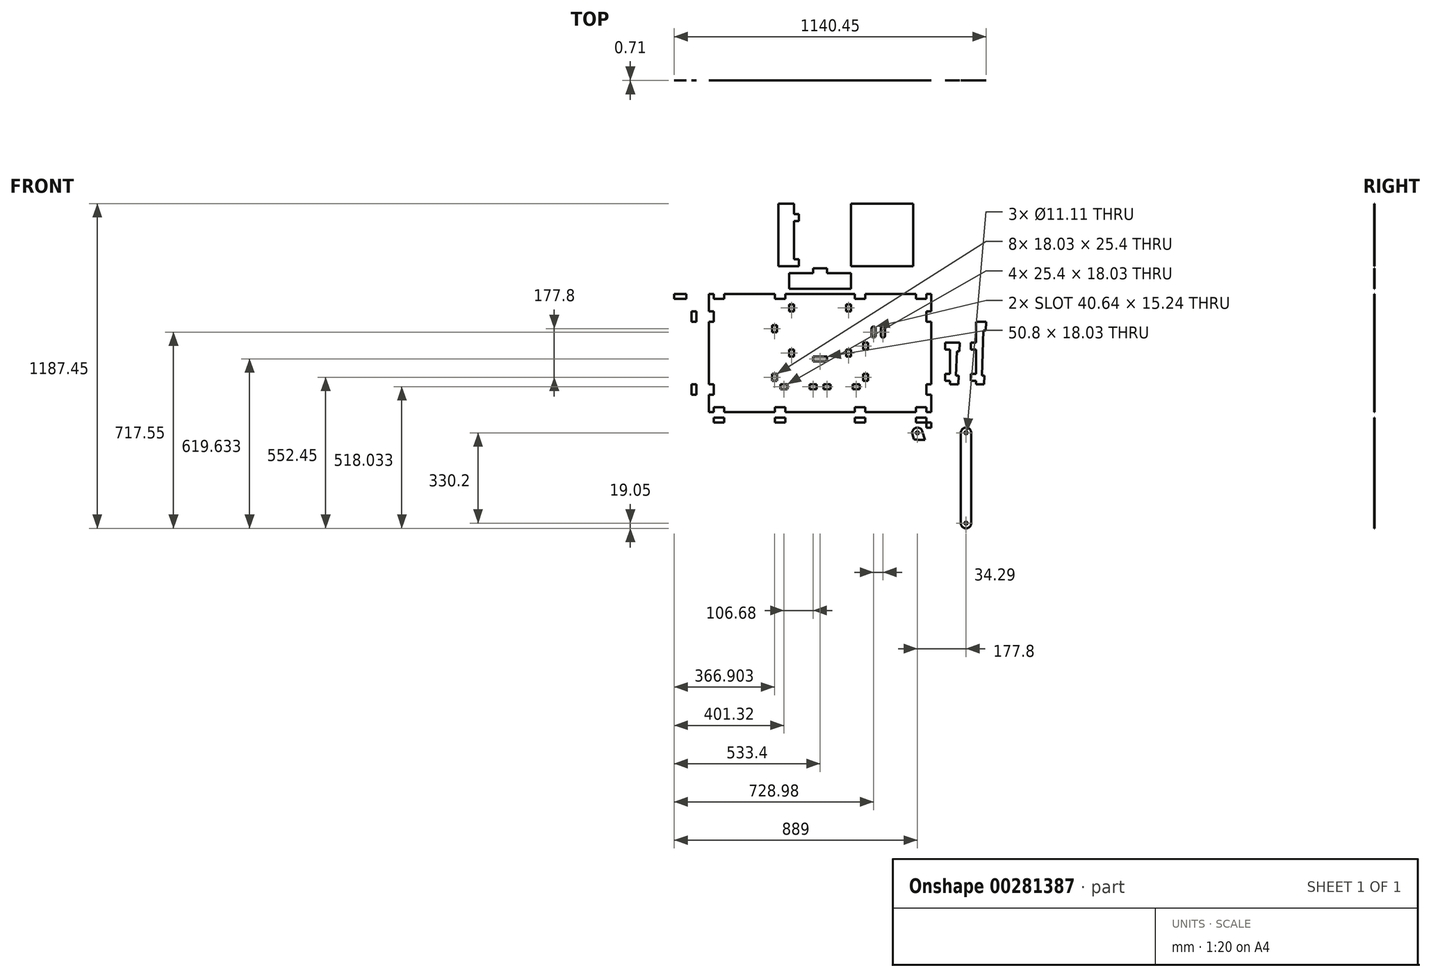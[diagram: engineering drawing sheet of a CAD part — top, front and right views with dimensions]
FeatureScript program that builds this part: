
annotation { "Feature Type Name" : "Feature", "Feature Type Description" : "" }
export const myFeature = defineFeature(function(context is Context, id is Id, definition is map)
    precondition{}
    {
        {
            assignVariable(context, id + "F0", {"name" : "ply34", "anyValue" : .71});
        }
        {
            var Q0;
            Q0=qCreatedBy(makeId("Front.planeOp"),FACE);
            var sketch = newSketch(context, id + "F1", { "sketchPlane" : qUnion([Q0])});
            skLineSegment(sketch, "E0.bottom", {"start": v(-406.4, 215.9) * mm, "end": v(406.4, 215.9) * mm});
            skLineSegment(sketch, "E0.top", {"start": v(-406.4, -215.9) * mm, "end": v(406.4, -215.9) * mm});
            skLineSegment(sketch, "E0.left", {"start": v(-406.4, 215.9) * mm, "end": v(-406.4, -215.9) * mm});
            skLineSegment(sketch, "E0.right", {"start": v(406.4, 215.9) * mm, "end": v(406.4, -215.9) * mm});
            skPoint(sketch, "E0.middle", {"position": v(0, 0) * mm});
            skLineSegment(sketch, "E1.bottom", {"start": v(-157.48, 114.3) * mm, "end": v(157.48, 114.3) * mm, "construction": true});
            skLineSegment(sketch, "E1.top", {"start": v(-157.48, -114.3) * mm, "end": v(157.48, -114.3) * mm, "construction": true});
            skLineSegment(sketch, "E1.left", {"start": v(-157.48, 114.3) * mm, "end": v(-157.48, -114.3) * mm, "construction": true});
            skLineSegment(sketch, "E1.right", {"start": v(157.48, 114.3) * mm, "end": v(157.48, -114.3) * mm, "construction": true});
            skLineSegment(sketch, "E2.bottom", {"start": v(-12.7, -114.3) * mm, "end": v(12.7, -114.3) * mm, "construction": true});
            skLineSegment(sketch, "E2.top", {"start": v(-12.7, 114.3) * mm, "end": v(12.7, 114.3) * mm, "construction": true});
            skLineSegment(sketch, "E2.left", {"start": v(-12.7, -114.3) * mm, "end": v(-12.7, 114.3) * mm, "construction": true});
            skLineSegment(sketch, "E2.right", {"start": v(12.7, -114.3) * mm, "end": v(12.7, 114.3) * mm, "construction": true});
            skLineSegment(sketch, "E3.bottom", {"start": v(157.48, 12.7) * mm, "end": v(175.51, 12.7) * mm});
            skLineSegment(sketch, "E3.top", {"start": v(157.48, 38.1) * mm, "end": v(175.51, 38.1) * mm});
            skLineSegment(sketch, "E3.left", {"start": v(157.48, 12.7) * mm, "end": v(157.48, 38.1) * mm});
            skLineSegment(sketch, "E3.right", {"start": v(175.51, 12.7) * mm, "end": v(175.51, 38.1) * mm});
            skLineSegment(sketch, "E4.bottom", {"start": v(157.48, -101.6) * mm, "end": v(175.51, -101.6) * mm});
            skLineSegment(sketch, "E4.top", {"start": v(157.48, -76.2) * mm, "end": v(175.51, -76.2) * mm});
            skLineSegment(sketch, "E4.left", {"start": v(157.48, -101.6) * mm, "end": v(157.48, -76.2) * mm});
            skLineSegment(sketch, "E4.right", {"start": v(175.51, -101.6) * mm, "end": v(175.51, -76.2) * mm});
            skLineSegment(sketch, "E5.bottom", {"start": v(-157.48, 101.6) * mm, "end": v(-175.51, 101.6) * mm});
            skLineSegment(sketch, "E5.top", {"start": v(-157.48, 76.2) * mm, "end": v(-175.51, 76.2) * mm});
            skLineSegment(sketch, "E5.left", {"start": v(-157.48, 101.6) * mm, "end": v(-157.48, 76.2) * mm});
            skLineSegment(sketch, "E5.right", {"start": v(-175.51, 101.6) * mm, "end": v(-175.51, 76.2) * mm});
            skLineSegment(sketch, "E6.bottom", {"start": v(-157.48, -76.2) * mm, "end": v(-175.51, -76.2) * mm});
            skLineSegment(sketch, "E6.top", {"start": v(-157.48, -101.6) * mm, "end": v(-175.51, -101.6) * mm});
            skLineSegment(sketch, "E6.left", {"start": v(-157.48, -76.2) * mm, "end": v(-157.48, -101.6) * mm});
            skLineSegment(sketch, "E6.right", {"start": v(-175.51, -76.2) * mm, "end": v(-175.51, -101.6) * mm});
            skLineSegment(sketch, "E7", {"start": v(195.58, 88.9) * mm, "end": v(195.58, 63.5) * mm});
            skLineSegment(sketch, "E8", {"start": v(229.87, 88.9) * mm, "end": v(229.87, 63.5) * mm});
            skArc(sketch, "E9.0.startCap", {"start": v(187.96, 88.9) * mm, "mid": v(195.58, 96.52) * mm, "end": v(203.2, 88.9) * mm});
            skArc(sketch, "E9.0.endCap", {"start": v(203.2, 63.5) * mm, "mid": v(195.58, 55.88) * mm, "end": v(187.96, 63.5) * mm});
            skLineSegment(sketch, "E9.0.left", {"start": v(203.2, 88.9) * mm, "end": v(203.2, 63.5) * mm});
            skLineSegment(sketch, "E9.0.right", {"start": v(187.96, 88.9) * mm, "end": v(187.96, 63.5) * mm});
            skArc(sketch, "E9.1.startCap", {"start": v(222.25, 88.9) * mm, "mid": v(229.87, 96.52) * mm, "end": v(237.49, 88.9) * mm});
            skArc(sketch, "E9.1.endCap", {"start": v(237.5, 63.5) * mm, "mid": v(229.87, 55.88) * mm, "end": v(222.25, 63.5) * mm});
            skLineSegment(sketch, "E9.1.left", {"start": v(237.49, 88.9) * mm, "end": v(237.49, 63.5) * mm});
            skLineSegment(sketch, "E9.1.right", {"start": v(222.25, 88.9) * mm, "end": v(222.25, 63.5) * mm});
            skLineSegment(sketch, "E10.bottom", {"start": v(-388.37, -215.9) * mm, "end": v(-350.27, -215.9) * mm});
            skLineSegment(sketch, "E10.top", {"start": v(-388.37, -197.87) * mm, "end": v(-350.27, -197.87) * mm});
            skLineSegment(sketch, "E10.left", {"start": v(-388.37, -215.9) * mm, "end": v(-388.37, -197.87) * mm});
            skLineSegment(sketch, "E10.right", {"start": v(-350.27, -215.9) * mm, "end": v(-350.27, -197.87) * mm});
            skLineSegment(sketch, "E11", {"start": v(0, -215.9) * mm, "end": v(0, 215.9) * mm, "construction": true});
            skLineSegment(sketch, "E12.bottom", {"start": v(-165.1, -215.9) * mm, "end": v(-127, -215.9) * mm});
            skLineSegment(sketch, "E12.top", {"start": v(-165.1, -197.87) * mm, "end": v(-127, -197.87) * mm});
            skLineSegment(sketch, "E12.left", {"start": v(-165.1, -215.9) * mm, "end": v(-165.1, -197.87) * mm});
            skLineSegment(sketch, "E12.right", {"start": v(-127, -215.9) * mm, "end": v(-127, -197.87) * mm});
            skLineSegment(sketch, "E13.MirrorCS", {"start": v(350.27, -215.9) * mm, "end": v(350.27, -197.87) * mm});
            skLineSegment(sketch, "E14.MirrorCS", {"start": v(127, -215.9) * mm, "end": v(127, -197.87) * mm});
            skLineSegment(sketch, "E15.MirrorCS", {"start": v(165.1, -215.9) * mm, "end": v(127, -215.9) * mm});
            skLineSegment(sketch, "E16.MirrorCS", {"start": v(388.37, -215.9) * mm, "end": v(388.37, -197.87) * mm});
            skLineSegment(sketch, "E17.MirrorCS", {"start": v(165.1, -197.87) * mm, "end": v(127, -197.87) * mm});
            skLineSegment(sketch, "E18.MirrorCS", {"start": v(165.1, -215.9) * mm, "end": v(165.1, -197.87) * mm});
            skLineSegment(sketch, "E19.MirrorCS", {"start": v(388.37, -197.87) * mm, "end": v(350.27, -197.87) * mm});
            skLineSegment(sketch, "E20.MirrorCS", {"start": v(388.37, -215.9) * mm, "end": v(350.27, -215.9) * mm});
            skLineSegment(sketch, "E21", {"start": v(0, 0) * mm, "end": v(-406.4, 0) * mm, "construction": true});
            skLineSegment(sketch, "E22.MirrorCS", {"start": v(165.1, 215.9) * mm, "end": v(165.1, 197.87) * mm});
            skLineSegment(sketch, "E23.MirrorCS", {"start": v(-165.1, 215.9) * mm, "end": v(-165.1, 197.87) * mm});
            skLineSegment(sketch, "E24.MirrorCS", {"start": v(-127, 215.9) * mm, "end": v(-127, 197.87) * mm});
            skLineSegment(sketch, "E25.MirrorCS", {"start": v(-388.37, 215.9) * mm, "end": v(-388.37, 197.87) * mm});
            skLineSegment(sketch, "E26.MirrorCS", {"start": v(127, 215.9) * mm, "end": v(127, 197.87) * mm});
            skLineSegment(sketch, "E27.MirrorCS", {"start": v(-350.27, 215.9) * mm, "end": v(-350.27, 197.87) * mm});
            skLineSegment(sketch, "E28.MirrorCS", {"start": v(350.27, 215.9) * mm, "end": v(350.27, 197.87) * mm});
            skLineSegment(sketch, "E29.MirrorCS", {"start": v(388.37, 215.9) * mm, "end": v(388.37, 197.87) * mm});
            skLineSegment(sketch, "E30.MirrorCS", {"start": v(165.1, 215.9) * mm, "end": v(127, 215.9) * mm});
            skLineSegment(sketch, "E31.MirrorCS", {"start": v(-388.37, 197.87) * mm, "end": v(-350.27, 197.87) * mm});
            skLineSegment(sketch, "E32.MirrorCS", {"start": v(388.37, 197.87) * mm, "end": v(350.27, 197.87) * mm});
            skLineSegment(sketch, "E33.MirrorCS", {"start": v(-165.1, 197.87) * mm, "end": v(-127, 197.87) * mm});
            skLineSegment(sketch, "E34.MirrorCS", {"start": v(-165.1, 215.9) * mm, "end": v(-127, 215.9) * mm});
            skLineSegment(sketch, "E35.MirrorCS", {"start": v(388.37, 215.9) * mm, "end": v(350.27, 215.9) * mm});
            skLineSegment(sketch, "E36.MirrorCS", {"start": v(-388.37, 215.9) * mm, "end": v(-350.27, 215.9) * mm});
            skLineSegment(sketch, "E37.MirrorCS", {"start": v(165.1, 197.87) * mm, "end": v(127, 197.87) * mm});
            skLineSegment(sketch, "E38.bottom", {"start": v(-406.4, 152.4) * mm, "end": v(-388.37, 152.4) * mm});
            skLineSegment(sketch, "E38.top", {"start": v(-406.4, 114.3) * mm, "end": v(-388.37, 114.3) * mm});
            skLineSegment(sketch, "E38.left", {"start": v(-406.4, 152.4) * mm, "end": v(-406.4, 114.3) * mm});
            skLineSegment(sketch, "E38.right", {"start": v(-388.37, 152.4) * mm, "end": v(-388.37, 114.3) * mm});
            skLineSegment(sketch, "E39.MirrorCS", {"start": v(-406.4, -152.4) * mm, "end": v(-388.37, -152.4) * mm});
            skLineSegment(sketch, "E40.MirrorCS", {"start": v(-406.4, -114.3) * mm, "end": v(-388.37, -114.3) * mm});
            skLineSegment(sketch, "E41.MirrorCS", {"start": v(-388.37, -152.4) * mm, "end": v(-388.37, -114.3) * mm});
            skLineSegment(sketch, "E42.MirrorCS", {"start": v(-406.4, -152.4) * mm, "end": v(-406.4, -114.3) * mm});
            skLineSegment(sketch, "E43.MirrorCS", {"start": v(406.4, -114.3) * mm, "end": v(388.37, -114.3) * mm});
            skLineSegment(sketch, "E44.MirrorCS", {"start": v(406.4, -152.4) * mm, "end": v(388.37, -152.4) * mm});
            skLineSegment(sketch, "E45.MirrorCS", {"start": v(406.4, 152.4) * mm, "end": v(388.37, 152.4) * mm});
            skLineSegment(sketch, "E46.MirrorCS", {"start": v(406.4, 114.3) * mm, "end": v(388.37, 114.3) * mm});
            skLineSegment(sketch, "E47.MirrorCS", {"start": v(406.4, -152.4) * mm, "end": v(406.4, -114.3) * mm});
            skLineSegment(sketch, "E48.MirrorCS", {"start": v(388.37, 152.4) * mm, "end": v(388.37, 114.3) * mm});
            skLineSegment(sketch, "E49.MirrorCS", {"start": v(388.37, -152.4) * mm, "end": v(388.37, -114.3) * mm});
            skLineSegment(sketch, "E50.MirrorCS", {"start": v(406.4, 152.4) * mm, "end": v(406.4, 114.3) * mm});
            skLineSegment(sketch, "E51.bottom", {"start": v(-12.7, -114.3) * mm, "end": v(-38.1, -114.3) * mm});
            skLineSegment(sketch, "E51.top", {"start": v(-12.7, -132.33) * mm, "end": v(-38.1, -132.33) * mm});
            skLineSegment(sketch, "E51.left", {"start": v(-12.7, -114.3) * mm, "end": v(-12.7, -132.33) * mm});
            skLineSegment(sketch, "E51.right", {"start": v(-38.1, -114.3) * mm, "end": v(-38.1, -132.33) * mm});
            skLineSegment(sketch, "E52.MirrorCS", {"start": v(38.1, -114.3) * mm, "end": v(38.1, -132.33) * mm});
            skLineSegment(sketch, "E53.MirrorCS", {"start": v(12.7, -114.3) * mm, "end": v(38.1, -114.3) * mm});
            skLineSegment(sketch, "E54.MirrorCS", {"start": v(12.7, -132.33) * mm, "end": v(38.1, -132.33) * mm});
            skLineSegment(sketch, "E55.MirrorCS", {"start": v(12.7, -114.3) * mm, "end": v(12.7, -132.33) * mm});
            skLineSegment(sketch, "E56.bottom", {"start": v(-144.78, -114.3) * mm, "end": v(-119.38, -114.3) * mm});
            skLineSegment(sketch, "E56.top", {"start": v(-144.78, -132.33) * mm, "end": v(-119.38, -132.33) * mm});
            skLineSegment(sketch, "E56.left", {"start": v(-144.78, -114.3) * mm, "end": v(-144.78, -132.33) * mm});
            skLineSegment(sketch, "E56.right", {"start": v(-119.38, -114.3) * mm, "end": v(-119.38, -132.33) * mm});
            skLineSegment(sketch, "E57.MirrorCS", {"start": v(144.78, -114.3) * mm, "end": v(119.38, -114.3) * mm});
            skLineSegment(sketch, "E58.MirrorCS", {"start": v(119.38, -114.3) * mm, "end": v(119.38, -132.33) * mm});
            skLineSegment(sketch, "E59.MirrorCS", {"start": v(144.78, -132.33) * mm, "end": v(119.38, -132.33) * mm});
            skLineSegment(sketch, "E60.MirrorCS", {"start": v(144.78, -114.3) * mm, "end": v(144.78, -132.33) * mm});
            skPoint(sketch, "E61.oppositeSnap0", {"position": v(166.5, -101.6) * mm});
            skLineSegment(sketch, "E61.bottom", {"start": v(457.2, -76.2) * mm, "end": v(475.23, -76.2) * mm});
            skLineSegment(sketch, "E61.top", {"start": v(457.2, -101.6) * mm, "end": v(475.23, -101.6) * mm});
            skLineSegment(sketch, "E61.left", {"start": v(457.2, -76.2) * mm, "end": v(457.2, -101.6) * mm});
            skLineSegment(sketch, "E61.right", {"start": v(475.23, -76.2) * mm, "end": v(475.23, -101.6) * mm});
            skLineSegment(sketch, "E62.bottom", {"start": v(457.2, 12.7) * mm, "end": v(475.23, 12.7) * mm});
            skLineSegment(sketch, "E62.top", {"start": v(457.2, 38.1) * mm, "end": v(475.23, 38.1) * mm});
            skLineSegment(sketch, "E62.left", {"start": v(457.2, 12.7) * mm, "end": v(457.2, 38.1) * mm});
            skLineSegment(sketch, "E62.right", {"start": v(475.23, 12.7) * mm, "end": v(475.23, 38.1) * mm});
            skLineSegment(sketch, "E63", {"start": v(475.23, 38.1) * mm, "end": v(475.23, -114.3) * mm});
            skLineSegment(sketch, "E64", {"start": v(475.23, -114.3) * mm, "end": v(495.87, -114.3) * mm});
            skLineSegment(sketch, "E65", {"start": v(495.87, -114.3) * mm, "end": v(501.16, 38.1) * mm});
            skLineSegment(sketch, "E66", {"start": v(503.8, 114.3) * mm, "end": v(475.23, 114.3) * mm, "construction": true});
            skLineSegment(sketch, "E67", {"start": v(475.23, 38.1) * mm, "end": v(501.16, 38.1) * mm});
            skLineSegment(sketch, "E68", {"start": v(501.16, 38.1) * mm, "end": v(503.8, 114.3) * mm, "construction": true});
            skLineSegment(sketch, "E69.bottom", {"start": v(551.43, 38.1) * mm, "end": v(569.47, 38.1) * mm});
            skLineSegment(sketch, "E69.top", {"start": v(551.43, 12.7) * mm, "end": v(569.47, 12.7) * mm});
            skLineSegment(sketch, "E69.left", {"start": v(551.43, 38.1) * mm, "end": v(551.43, 12.7) * mm});
            skLineSegment(sketch, "E69.right", {"start": v(569.47, 38.1) * mm, "end": v(569.47, 12.7) * mm});
            skLineSegment(sketch, "E70.bottom", {"start": v(551.43, -76.2) * mm, "end": v(569.47, -76.2) * mm});
            skLineSegment(sketch, "E70.top", {"start": v(551.43, -101.6) * mm, "end": v(569.47, -101.6) * mm});
            skLineSegment(sketch, "E70.left", {"start": v(551.43, -76.2) * mm, "end": v(551.43, -101.6) * mm});
            skLineSegment(sketch, "E70.right", {"start": v(569.47, -76.2) * mm, "end": v(569.47, -101.6) * mm});
            skLineSegment(sketch, "E71", {"start": v(569.47, 114.3) * mm, "end": v(569.47, -114.3) * mm});
            skLineSegment(sketch, "E72", {"start": v(569.47, -114.3) * mm, "end": v(590.1, -114.3) * mm});
            skLineSegment(sketch, "E73", {"start": v(590.1, -114.3) * mm, "end": v(598.04, 114.3) * mm});
            skLineSegment(sketch, "E74", {"start": v(598.04, 114.3) * mm, "end": v(569.47, 114.3) * mm});
            skLineSegment(sketch, "E75", {"start": v(501.16, 38.1) * mm, "end": v(510.17, 37.79) * mm});
            skLineSegment(sketch, "E76", {"start": v(510.17, 37.79) * mm, "end": v(509.07, 6.06) * mm});
            skLineSegment(sketch, "E77", {"start": v(509.07, 6.06) * mm, "end": v(500.06, 6.37) * mm});
            skLineSegment(sketch, "E78", {"start": v(495.87, -114.3) * mm, "end": v(504.88, -114.61) * mm});
            skLineSegment(sketch, "E79", {"start": v(504.88, -114.61) * mm, "end": v(505.98, -82.88) * mm});
            skLineSegment(sketch, "E80", {"start": v(505.98, -82.88) * mm, "end": v(496.97, -82.57) * mm});
            skLineSegment(sketch, "E81", {"start": v(598.04, 114.3) * mm, "end": v(607.05, 113.99) * mm});
            skLineSegment(sketch, "E82", {"start": v(607.05, 113.99) * mm, "end": v(605.95, 82.26) * mm});
            skLineSegment(sketch, "E83", {"start": v(605.95, 82.26) * mm, "end": v(596.94, 82.57) * mm});
            skLineSegment(sketch, "E84", {"start": v(590.1, -114.3) * mm, "end": v(599.12, -114.61) * mm});
            skLineSegment(sketch, "E85", {"start": v(599.12, -114.61) * mm, "end": v(600.22, -82.88) * mm});
            skLineSegment(sketch, "E86", {"start": v(600.22, -82.88) * mm, "end": v(591.2, -82.57) * mm});
            skLineSegment(sketch, "E87.bottom", {"start": v(-533.4, 215.9) * mm, "end": v(-469.9, 215.9) * mm});
            skLineSegment(sketch, "E87.top", {"start": v(-533.4, -215.9) * mm, "end": v(-469.9, -215.9) * mm});
            skLineSegment(sketch, "E87.left", {"start": v(-533.4, 215.9) * mm, "end": v(-533.4, -215.9) * mm});
            skLineSegment(sketch, "E87.right", {"start": v(-469.9, 215.9) * mm, "end": v(-469.9, -215.9) * mm});
            skLineSegment(sketch, "E88.bottom", {"start": v(-533.4, 215.9) * mm, "end": v(-488.95, 215.9) * mm});
            skLineSegment(sketch, "E88.top", {"start": v(-533.4, 197.87) * mm, "end": v(-488.95, 197.87) * mm});
            skLineSegment(sketch, "E88.left", {"start": v(-533.4, 215.9) * mm, "end": v(-533.4, 197.87) * mm});
            skLineSegment(sketch, "E88.right", {"start": v(-488.95, 215.9) * mm, "end": v(-488.95, 197.87) * mm});
            skLineSegment(sketch, "E89", {"start": v(-469.9, 152.4) * mm, "end": v(-451.87, 152.4) * mm});
            skLineSegment(sketch, "E90", {"start": v(-451.87, 152.4) * mm, "end": v(-451.87, 114.3) * mm});
            skLineSegment(sketch, "E91", {"start": v(-451.87, 114.3) * mm, "end": v(-469.9, 114.3) * mm});
            skLineSegment(sketch, "E92", {"start": v(-469.9, -114.3) * mm, "end": v(-451.87, -114.3) * mm});
            skLineSegment(sketch, "E93", {"start": v(-451.87, -114.3) * mm, "end": v(-451.87, -152.4) * mm});
            skLineSegment(sketch, "E94", {"start": v(-451.87, -152.4) * mm, "end": v(-469.9, -152.4) * mm});
            skPoint(sketch, "E95.oppositeSnap0", {"position": v(-501.65, -215.9) * mm});
            skLineSegment(sketch, "E95.bottom", {"start": v(-533.4, -215.9) * mm, "end": v(-501.65, -215.9) * mm});
            skLineSegment(sketch, "E95.top", {"start": v(-533.4, -197.87) * mm, "end": v(-501.65, -197.87) * mm});
            skLineSegment(sketch, "E95.left", {"start": v(-533.4, -215.9) * mm, "end": v(-533.4, -197.87) * mm});
            skLineSegment(sketch, "E95.right", {"start": v(-501.65, -215.9) * mm, "end": v(-501.65, -197.87) * mm});
            skLineSegment(sketch, "E96", {"start": v(-406.4, -254) * mm, "end": v(406.4, -254) * mm});
            skLineSegment(sketch, "E97", {"start": v(406.4, -254) * mm, "end": v(406.4, -317.5) * mm});
            skLineSegment(sketch, "E98", {"start": v(406.4, -317.5) * mm, "end": v(355.6, -317.5) * mm});
            skLineSegment(sketch, "E99", {"start": v(-406.4, -254) * mm, "end": v(-406.4, -317.5) * mm});
            skLineSegment(sketch, "E100", {"start": v(-406.4, -317.5) * mm, "end": v(-355.6, -317.5) * mm});
            skArc(sketch, "E101", {"start": v(355.6, -317.5) * mm, "mid": v(0, -292.1) * mm, "end": v(-355.6, -317.5) * mm});
            skLineSegment(sketch, "E102", {"start": v(-388.37, -254) * mm, "end": v(-388.37, -235.97) * mm});
            skLineSegment(sketch, "E103", {"start": v(-388.37, -235.97) * mm, "end": v(-350.27, -235.97) * mm});
            skLineSegment(sketch, "E104", {"start": v(-350.27, -235.97) * mm, "end": v(-350.27, -254) * mm});
            skLineSegment(sketch, "E105", {"start": v(-165.1, -254) * mm, "end": v(-165.1, -235.97) * mm});
            skLineSegment(sketch, "E106", {"start": v(-165.1, -235.97) * mm, "end": v(-127, -235.97) * mm});
            skLineSegment(sketch, "E107", {"start": v(-127, -235.97) * mm, "end": v(-127, -254) * mm});
            skLineSegment(sketch, "E108", {"start": v(127, -254) * mm, "end": v(127, -235.97) * mm});
            skLineSegment(sketch, "E109", {"start": v(127, -235.97) * mm, "end": v(165.1, -235.97) * mm});
            skLineSegment(sketch, "E110", {"start": v(165.1, -235.97) * mm, "end": v(165.1, -254) * mm});
            skLineSegment(sketch, "E111", {"start": v(350.27, -254) * mm, "end": v(350.27, -235.97) * mm});
            skLineSegment(sketch, "E112", {"start": v(350.27, -235.97) * mm, "end": v(388.37, -235.97) * mm});
            skLineSegment(sketch, "E113", {"start": v(388.37, -235.97) * mm, "end": v(388.37, -254) * mm});
            skLineSegment(sketch, "E114.bottom", {"start": v(-406.4, -254) * mm, "end": v(-388.37, -254) * mm});
            skLineSegment(sketch, "E114.top", {"start": v(-406.4, -273.05) * mm, "end": v(-388.37, -273.05) * mm});
            skLineSegment(sketch, "E114.left", {"start": v(-406.4, -254) * mm, "end": v(-406.4, -273.05) * mm});
            skLineSegment(sketch, "E114.right", {"start": v(-388.37, -254) * mm, "end": v(-388.37, -273.05) * mm});
            skLineSegment(sketch, "E115.bottom", {"start": v(406.4, -254) * mm, "end": v(388.37, -254) * mm});
            skLineSegment(sketch, "E115.top", {"start": v(406.4, -273.05) * mm, "end": v(388.37, -273.05) * mm});
            skLineSegment(sketch, "E115.left", {"start": v(406.4, -254) * mm, "end": v(406.4, -273.05) * mm});
            skLineSegment(sketch, "E115.right", {"start": v(388.37, -254) * mm, "end": v(388.37, -273.05) * mm});
            skCircle(sketch, "E116", {"center": v(355.6, -292.1) * mm, "radius": 5.56 * mm});
            skCircle(sketch, "E117", {"center": v(355.6, -292.1) * mm, "radius": 19.05 * mm});
            skLineSegment(sketch, "E118", {"start": v(373.86, -286.67) * mm, "end": v(467.99, -603.17) * mm});
            skLineSegment(sketch, "E119", {"start": v(373.86, -286.67) * mm, "end": v(337.34, -297.53) * mm});
            skLineSegment(sketch, "E120", {"start": v(337.34, -297.53) * mm, "end": v(431.47, -614.03) * mm});
            skLineSegment(sketch, "E121", {"start": v(431.47, -614.03) * mm, "end": v(467.99, -603.17) * mm});
            skArc(sketch, "E122", {"start": v(-533.4, -152.4) * mm, "mid": v(-495.3, 0) * mm, "end": v(-533.4, 152.4) * mm});
            skLineSegment(sketch, "E123", {"start": v(388.37, -273.05) * mm, "end": v(388.37, -317.5) * mm, "construction": true});
            skArc(sketch, "E124", {"start": v(431.47, -614.03) * mm, "mid": v(455.16, -626.86) * mm, "end": v(467.99, -603.17) * mm});
            skArc(sketch, "E125", {"start": v(552.45, -292.1) * mm, "mid": v(533.4, -273.05) * mm, "end": v(514.35, -292.1) * mm});
            skLineSegment(sketch, "E126", {"start": v(514.35, -292.1) * mm, "end": v(514.35, -622.3) * mm});
            skLineSegment(sketch, "E127", {"start": v(552.45, -292.1) * mm, "end": v(552.45, -622.3) * mm});
            skArc(sketch, "E128", {"start": v(514.35, -622.3) * mm, "mid": v(533.4, -641.35) * mm, "end": v(552.45, -622.3) * mm});
            skCircle(sketch, "E129", {"center": v(533.4, -292.1) * mm, "radius": 5.56 * mm});
            skCircle(sketch, "E130", {"center": v(533.4, -622.3) * mm, "radius": 5.56 * mm});
            skLineSegment(sketch, "E131.bottom", {"start": v(-95.25, 215.9) * mm, "end": v(95.25, 215.9) * mm, "construction": true});
            skLineSegment(sketch, "E131.top", {"start": v(-95.25, -12.7) * mm, "end": v(95.25, -12.7) * mm, "construction": true});
            skLineSegment(sketch, "E131.left", {"start": v(-95.25, 215.9) * mm, "end": v(-95.25, -12.7) * mm, "construction": true});
            skLineSegment(sketch, "E131.right", {"start": v(95.25, 215.9) * mm, "end": v(95.25, -12.7) * mm, "construction": true});
            skPoint(sketch, "E131.middle", {"position": v(0, 101.6) * mm});
            skLineSegment(sketch, "E132.bottom", {"start": v(-95.25, 177.8) * mm, "end": v(-113.28, 177.8) * mm});
            skLineSegment(sketch, "E132.top", {"start": v(-95.25, 152.4) * mm, "end": v(-113.28, 152.4) * mm});
            skLineSegment(sketch, "E132.left", {"start": v(-95.25, 177.8) * mm, "end": v(-95.25, 152.4) * mm});
            skLineSegment(sketch, "E132.right", {"start": v(-113.28, 177.8) * mm, "end": v(-113.28, 152.4) * mm});
            skLineSegment(sketch, "E133.bottom", {"start": v(95.25, 152.4) * mm, "end": v(113.28, 152.4) * mm});
            skLineSegment(sketch, "E133.top", {"start": v(95.25, 177.8) * mm, "end": v(113.28, 177.8) * mm});
            skLineSegment(sketch, "E133.left", {"start": v(95.25, 152.4) * mm, "end": v(95.25, 177.8) * mm});
            skLineSegment(sketch, "E133.right", {"start": v(113.28, 152.4) * mm, "end": v(113.28, 177.8) * mm});
            skLineSegment(sketch, "E134.bottom", {"start": v(-95.25, -12.7) * mm, "end": v(-113.28, -12.7) * mm});
            skLineSegment(sketch, "E134.top", {"start": v(-95.25, 12.7) * mm, "end": v(-113.28, 12.7) * mm});
            skLineSegment(sketch, "E134.left", {"start": v(-95.25, -12.7) * mm, "end": v(-95.25, 12.7) * mm});
            skLineSegment(sketch, "E134.right", {"start": v(-113.28, -12.7) * mm, "end": v(-113.28, 12.7) * mm});
            skLineSegment(sketch, "E135.bottom", {"start": v(95.25, -12.7) * mm, "end": v(113.28, -12.7) * mm});
            skLineSegment(sketch, "E135.top", {"start": v(95.25, 12.7) * mm, "end": v(113.28, 12.7) * mm});
            skLineSegment(sketch, "E135.left", {"start": v(95.25, -12.7) * mm, "end": v(95.25, 12.7) * mm});
            skLineSegment(sketch, "E135.right", {"start": v(113.28, -12.7) * mm, "end": v(113.28, 12.7) * mm});
            skLineSegment(sketch, "E136.bottom", {"start": v(-25.4, -12.7) * mm, "end": v(25.4, -12.7) * mm});
            skLineSegment(sketch, "E136.top", {"start": v(-25.4, -30.73) * mm, "end": v(25.4, -30.73) * mm});
            skLineSegment(sketch, "E136.left", {"start": v(-25.4, -12.7) * mm, "end": v(-25.4, -30.73) * mm});
            skLineSegment(sketch, "E136.right", {"start": v(25.4, -12.7) * mm, "end": v(25.4, -30.73) * mm});
            skPoint(sketch, "E136.middle", {"position": v(0, -21.72) * mm});
            skLineSegment(sketch, "E137.bottom", {"start": v(-95.25, 317.5) * mm, "end": v(-152.4, 317.5) * mm});
            skLineSegment(sketch, "E137.top", {"start": v(-95.25, 546.1) * mm, "end": v(-152.4, 546.1) * mm});
            skLineSegment(sketch, "E137.left", {"start": v(-95.25, 317.5) * mm, "end": v(-95.25, 546.1) * mm});
            skLineSegment(sketch, "E137.right", {"start": v(-152.4, 317.5) * mm, "end": v(-152.4, 546.1) * mm});
            skLineSegment(sketch, "E138", {"start": v(-95.25, 508) * mm, "end": v(-77.22, 508) * mm});
            skLineSegment(sketch, "E139", {"start": v(-77.22, 508) * mm, "end": v(-77.22, 482.6) * mm});
            skLineSegment(sketch, "E140", {"start": v(-77.22, 482.6) * mm, "end": v(-95.25, 482.6) * mm});
            skLineSegment(sketch, "E141", {"start": v(-95.25, 317.5) * mm, "end": v(-77.22, 317.5) * mm});
            skLineSegment(sketch, "E142", {"start": v(-77.22, 317.5) * mm, "end": v(-77.22, 342.9) * mm});
            skLineSegment(sketch, "E143", {"start": v(-77.22, 342.9) * mm, "end": v(-95.25, 342.9) * mm});
            skLineSegment(sketch, "E144.bottom", {"start": v(-113.28, 234.95) * mm, "end": v(113.28, 234.95) * mm});
            skLineSegment(sketch, "E144.top", {"start": v(-113.28, 292.1) * mm, "end": v(113.28, 292.1) * mm});
            skLineSegment(sketch, "E144.left", {"start": v(-113.28, 234.95) * mm, "end": v(-113.28, 292.1) * mm});
            skLineSegment(sketch, "E144.right", {"start": v(113.28, 234.95) * mm, "end": v(113.28, 292.1) * mm});
            skLineSegment(sketch, "E145", {"start": v(-25.4, 292.1) * mm, "end": v(-25.4, 310.13) * mm});
            skLineSegment(sketch, "E146", {"start": v(-25.4, 310.13) * mm, "end": v(25.4, 310.13) * mm});
            skLineSegment(sketch, "E147", {"start": v(25.4, 310.13) * mm, "end": v(25.4, 292.1) * mm});
            skCircle(sketch, "E148.MirrorC", {"center": v(-355.6, -292.1) * mm, "radius": 5.56 * mm});
            skLineSegment(sketch, "E149.bottom", {"start": v(113.28, 546.1) * mm, "end": v(339.85, 546.1) * mm});
            skLineSegment(sketch, "E149.top", {"start": v(113.28, 317.5) * mm, "end": v(339.85, 317.5) * mm});
            skLineSegment(sketch, "E149.left", {"start": v(113.28, 546.1) * mm, "end": v(113.28, 317.5) * mm});
            skLineSegment(sketch, "E149.right", {"start": v(339.85, 546.1) * mm, "end": v(339.85, 317.5) * mm});
            skSolve(sketch);
        }
        {
            var Q0;
            {var subQ3=sQuery(id+"F1.wireOp",EDGE,"E137.bottom");Q0=makeQuery(id+"F1.imprint","IMPRINT",FACE,{"disambiguationData":[TD([[makeQuery(id+"F1.imprint","IMPRINT",EDGE,{"derivedFrom":subQ3}),-1.0]])]});}
            var Q1;
            {var subQ0=sQuery(id+"F1.wireOp",EDGE,"E138");Q1=makeQuery(id+"F1.imprint","IMPRINT",FACE,{"disambiguationData":[TD([[makeQuery(id+"F1.imprint","IMPRINT",EDGE,{"derivedFrom":subQ0}),-1.0]])]});}
            var Q2;
            {var subQ0=sQuery(id+"F1.wireOp",EDGE,"E141");Q2=makeQuery(id+"F1.imprint","IMPRINT",FACE,{"disambiguationData":[TD([[makeQuery(id+"F1.imprint","IMPRINT",EDGE,{"derivedFrom":subQ0}),1.0]])]});}
            var Q3;
            {var subQ0=sQuery(id+"F1.wireOp",EDGE,"E145");Q3=makeQuery(id+"F1.imprint","IMPRINT",FACE,{"disambiguationData":[TD([[makeQuery(id+"F1.imprint","IMPRINT",EDGE,{"derivedFrom":subQ0}),-1.0]])]});}
            var Q4;
            Q4=makeQuery(id+"F1.imprint","IMPRINT",FACE,{"disambiguationData":[TD([[makeQuery(id+"F1.imprint","IMPRINT",EDGE,{"derivedFrom":sQuery(id+"F1.wireOp",EDGE,"E144.bottom")}),1.0]])]});
            var Q5;
            Q5=makeQuery(id+"F1.imprint","IMPRINT",FACE,{"disambiguationData":[TD([[makeQuery(id+"F1.imprint","IMPRINT",EDGE,{"derivedFrom":sQuery(id+"F1.wireOp",EDGE,"E3.bottom")}),-1.0]])]});
            var Q6;
            {var subQ6=sQuery(id+"F1.wireOp",EDGE,"E87.bottom");Q6=makeQuery(id+"F1.imprint","IMPRINT",FACE,{"disambiguationData":[TD([[makeQuery(id+"F1.imprint","IMPRINT",EDGE,{"derivedFrom":subQ6}),-1.0]])]});}
            var Q7;
            {var subQ0=sQuery(id+"F1.wireOp",EDGE,"E89");Q7=makeQuery(id+"F1.imprint","IMPRINT",FACE,{"disambiguationData":[TD([[makeQuery(id+"F1.imprint","IMPRINT",EDGE,{"derivedFrom":subQ0}),-1.0]])]});}
            var Q8;
            {var subQ0=sQuery(id+"F1.wireOp",EDGE,"E92");Q8=makeQuery(id+"F1.imprint","IMPRINT",FACE,{"disambiguationData":[TD([[makeQuery(id+"F1.imprint","IMPRINT",EDGE,{"derivedFrom":subQ0}),-1.0]])]});}
            var Q9;
            {var subQ0=sQuery(id+"F1.wireOp",EDGE,"E62.bottom");Q9=makeQuery(id+"F1.imprint","IMPRINT",FACE,{"disambiguationData":[TD([[makeQuery(id+"F1.imprint","IMPRINT",EDGE,{"derivedFrom":subQ0}),1.0]])]});}
            var Q10;
            {var subQ2=sQuery(id+"F1.wireOp",EDGE,"E64");Q10=makeQuery(id+"F1.imprint","IMPRINT",FACE,{"disambiguationData":[TD([[makeQuery(id+"F1.imprint","IMPRINT",EDGE,{"derivedFrom":subQ2}),1.0]])]});}
            var Q11;
            {var subQ0=sQuery(id+"F1.wireOp",EDGE,"E75");Q11=makeQuery(id+"F1.imprint","IMPRINT",FACE,{"disambiguationData":[TD([[makeQuery(id+"F1.imprint","IMPRINT",EDGE,{"derivedFrom":subQ0}),-1.0]])]});}
            var Q12;
            {var subQ0=sQuery(id+"F1.wireOp",EDGE,"E78");Q12=makeQuery(id+"F1.imprint","IMPRINT",FACE,{"disambiguationData":[TD([[makeQuery(id+"F1.imprint","IMPRINT",EDGE,{"derivedFrom":subQ0}),1.0]])]});}
            var Q13;
            {var subQ0=sQuery(id+"F1.wireOp",EDGE,"E61.bottom");Q13=makeQuery(id+"F1.imprint","IMPRINT",FACE,{"disambiguationData":[TD([[makeQuery(id+"F1.imprint","IMPRINT",EDGE,{"derivedFrom":subQ0}),-1.0]])]});}
            var Q14;
            {var subQ0=sQuery(id+"F1.wireOp",EDGE,"E70.bottom");Q14=makeQuery(id+"F1.imprint","IMPRINT",FACE,{"disambiguationData":[TD([[makeQuery(id+"F1.imprint","IMPRINT",EDGE,{"derivedFrom":subQ0}),-1.0]])]});}
            var Q15;
            {var subQ0=sQuery(id+"F1.wireOp",EDGE,"E69.bottom");Q15=makeQuery(id+"F1.imprint","IMPRINT",FACE,{"disambiguationData":[TD([[makeQuery(id+"F1.imprint","IMPRINT",EDGE,{"derivedFrom":subQ0}),-1.0]])]});}
            var Q16;
            {var subQ0=sQuery(id+"F1.wireOp",EDGE,"E81");Q16=makeQuery(id+"F1.imprint","IMPRINT",FACE,{"disambiguationData":[TD([[makeQuery(id+"F1.imprint","IMPRINT",EDGE,{"derivedFrom":subQ0}),-1.0]])]});}
            var Q17;
            {var subQ0=sQuery(id+"F1.wireOp",EDGE,"E84");Q17=makeQuery(id+"F1.imprint","IMPRINT",FACE,{"disambiguationData":[TD([[makeQuery(id+"F1.imprint","IMPRINT",EDGE,{"derivedFrom":subQ0}),1.0]])]});}
            var Q18;
            {var subQ6=sQuery(id+"F1.wireOp",EDGE,"E72");Q18=makeQuery(id+"F1.imprint","IMPRINT",FACE,{"disambiguationData":[TD([[makeQuery(id+"F1.imprint","IMPRINT",EDGE,{"derivedFrom":subQ6}),1.0]])]});}
            var Q19;
            {var subQ0=sQuery(id+"F1.wireOp",EDGE,"E102");Q19=makeQuery(id+"F1.imprint","IMPRINT",FACE,{"disambiguationData":[TD([[makeQuery(id+"F1.imprint","IMPRINT",EDGE,{"derivedFrom":subQ0}),-1.0]])]});}
            var Q20;
            {var subQ2=sQuery(id+"F1.wireOp",EDGE,"E97");Q20=makeQuery(id+"F1.imprint","IMPRINT",FACE,{"disambiguationData":[TD([[makeQuery(id+"F1.imprint","IMPRINT",EDGE,{"derivedFrom":subQ2}),-1.0]])]});}
            var Q21;
            {var subQ0=sQuery(id+"F1.wireOp",EDGE,"E105");Q21=makeQuery(id+"F1.imprint","IMPRINT",FACE,{"disambiguationData":[TD([[makeQuery(id+"F1.imprint","IMPRINT",EDGE,{"derivedFrom":subQ0}),-1.0]])]});}
            var Q22;
            {var subQ0=sQuery(id+"F1.wireOp",EDGE,"E108");Q22=makeQuery(id+"F1.imprint","IMPRINT",FACE,{"disambiguationData":[TD([[makeQuery(id+"F1.imprint","IMPRINT",EDGE,{"derivedFrom":subQ0}),-1.0]])]});}
            var Q23;
            {var subQ2=sQuery(id+"F1.wireOp",EDGE,"E111");Q23=makeQuery(id+"F1.imprint","IMPRINT",FACE,{"disambiguationData":[TD([[makeQuery(id+"F1.imprint","IMPRINT",EDGE,{"derivedFrom":subQ2}),-1.0]])]});}
            var Q24;
            {var subQ4=sQuery(id+"F1.wireOp",EDGE,"E98");var subQ8=sQuery(id+"F1.wireOp",EDGE,"E101");var subQ9=makeQuery(id+"F1.imprint","INTERSECT",VERTEX,{"derivedFrom":[subQ4,subQ8]});Q24=makeQuery(id+"F1.imprint","IMPRINT",FACE,{"disambiguationData":[TD([[makeQuery(id+"F1.imprint","IMPRINT",EDGE,{"disambiguationData":[TD([[subQ9,1.0]])],"derivedFrom":subQ4}),-1.0]])]});}
            var Q25;
            {var subQ0=sQuery(id+"F1.wireOp",EDGE,"E119");var subQ1=sQuery(id+"F1.wireOp",EDGE,"E116");var subQ2=makeQuery(id+"F1.imprint","INTERSECT",VERTEX,{"disambiguationData":[OD(0.0)],"derivedFrom":[subQ1,subQ0]});Q25=makeQuery(id+"F1.imprint","IMPRINT",FACE,{"disambiguationData":[TD([[makeQuery(id+"F1.imprint","IMPRINT",EDGE,{"disambiguationData":[TD([[subQ2,1.0]])],"derivedFrom":subQ1}),-1.0]])]});}
            var Q26;
            {var subQ0=sQuery(id+"F1.wireOp",EDGE,"E119");var subQ1=sQuery(id+"F1.wireOp",EDGE,"E116");var subQ2=makeQuery(id+"F1.imprint","INTERSECT",VERTEX,{"disambiguationData":[OD(0.0)],"derivedFrom":[subQ1,subQ0]});Q26=makeQuery(id+"F1.imprint","IMPRINT",FACE,{"disambiguationData":[TD([[makeQuery(id+"F1.imprint","IMPRINT",EDGE,{"disambiguationData":[TD([[subQ2,-1.0]])],"derivedFrom":subQ1}),-1.0]])]});}
            var Q27;
            Q27=makeQuery(id+"F1.imprint","IMPRINT",FACE,{"disambiguationData":[TD([[makeQuery(id+"F1.imprint","IMPRINT",EDGE,{"derivedFrom":sQuery(id+"F1.wireOp",EDGE,"E125")}),1.0]])]});
            var Q28;
            Q28=makeQuery(id+"F1.imprint","IMPRINT",FACE,{"disambiguationData":[TD([[makeQuery(id+"F1.imprint","IMPRINT",EDGE,{"derivedFrom":sQuery(id+"F1.wireOp",EDGE,"E149.bottom")}),-1.0]])]});
            extrude(context, id + "F2", {"entities" : qUnion([Q0, Q1, Q2, Q3, Q4, Q5, Q6, Q7, Q8, Q9, Q10, Q11, Q12, Q13, Q14, Q15, Q16, Q17, Q18, Q19, Q20, Q21, Q22, Q23, Q24, Q25, Q26, Q27, Q28]), "depth" : (getVariable(context, 'ply34')) * mm});
        }
    });
